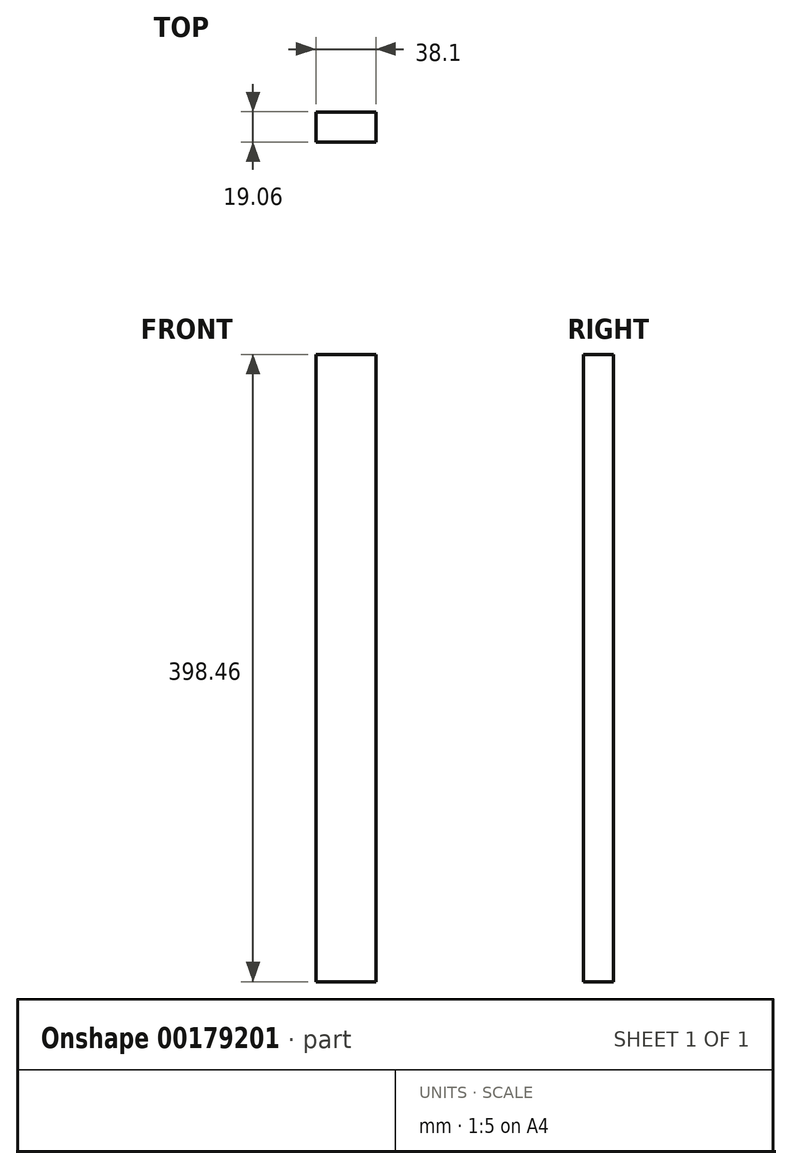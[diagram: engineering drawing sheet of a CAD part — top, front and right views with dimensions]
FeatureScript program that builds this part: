
annotation { "Feature Type Name" : "Feature", "Feature Type Description" : "" }
export const myFeature = defineFeature(function(context is Context, id is Id, definition is map)
    precondition{}
    {
        {
            var Q0;
            Q0=qCreatedBy(makeId("Front.planeOp"),FACE);
            var sketch = newSketch(context, id + "F0", { "sketchPlane" : qUnion([Q0])});
            skLineSegment(sketch, "E0.bottom", {"start": v(-32, 199.23) * mm, "end": v(6.1, 199.23) * mm});
            skLineSegment(sketch, "E0.top", {"start": v(-32, -199.23) * mm, "end": v(6.1, -199.23) * mm});
            skLineSegment(sketch, "E0.left", {"start": v(-32, 199.23) * mm, "end": v(-32, -199.23) * mm});
            skLineSegment(sketch, "E0.right", {"start": v(6.1, 199.23) * mm, "end": v(6.1, -199.23) * mm});
            skLineSegment(sketch, "E1", {"start": v(-32, 0) * mm, "end": v(6.1, 0) * mm});
            skSolve(sketch);
        }
        {
            var Q0;
            {var subQ0=sQuery(id+"F0.wireOp",EDGE,"E0.bottom");Q0=makeQuery(id+"F0.imprint","IMPRINT",FACE,{"disambiguationData":[TD([[makeQuery(id+"F0.imprint","IMPRINT",EDGE,{"derivedFrom":subQ0}),-1.0]])]});}
            var Q1;
            {var subQ0=sQuery(id+"F0.wireOp",EDGE,"E0.top");Q1=makeQuery(id+"F0.imprint","IMPRINT",FACE,{"disambiguationData":[TD([[makeQuery(id+"F0.imprint","IMPRINT",EDGE,{"derivedFrom":subQ0}),1.0]])]});}
            extrude(context, id + "F1", {"entities" : qUnion([Q0, Q1]), "depth" : 19.05 * mm, "symmetric" : true});
        }
    });
